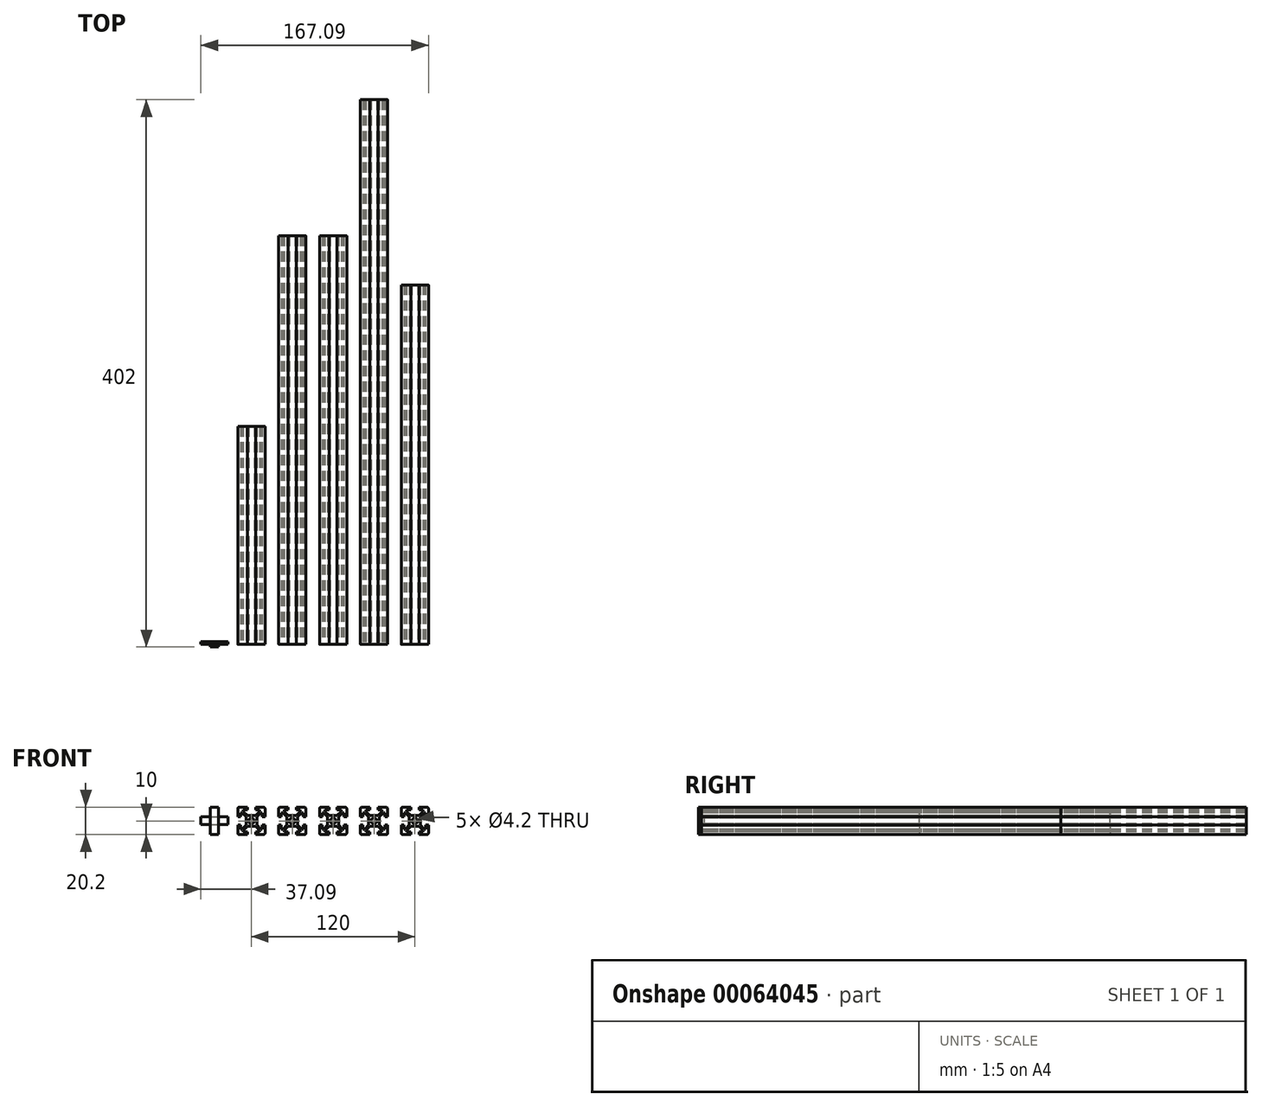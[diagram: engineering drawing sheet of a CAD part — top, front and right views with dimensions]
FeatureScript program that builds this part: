
annotation { "Feature Type Name" : "Feature", "Feature Type Description" : "" }
export const myFeature = defineFeature(function(context is Context, id is Id, definition is map)
    precondition{}
    {
        {
            var Q0;
            Q0=qCreatedBy(makeId("Front.planeOp"),FACE);
            var sketch = newSketch(context, id + "F0", { "sketchPlane" : qUnion([Q0])});
            skLineSegment(sketch, "E0", {"start": v(0, 4) * mm, "end": v(3, 4) * mm});
            skLineSegment(sketch, "E1", {"start": v(3, 4) * mm, "end": v(6, 7) * mm});
            skLineSegment(sketch, "E2", {"start": v(6, 7) * mm, "end": v(6, 8) * mm});
            skLineSegment(sketch, "E3", {"start": v(6, 8) * mm, "end": v(3, 8) * mm});
            skLineSegment(sketch, "E4", {"start": v(3, 8) * mm, "end": v(3, 10) * mm});
            skLineSegment(sketch, "E5", {"start": v(3, 10) * mm, "end": v(9, 10) * mm});
            skLineSegment(sketch, "E6", {"start": v(0, 0) * mm, "end": v(12.93, 12.93) * mm, "construction": true});
            skLineSegment(sketch, "E7.MirrorCS", {"start": v(4, 0) * mm, "end": v(4, 3) * mm});
            skLineSegment(sketch, "E8.MirrorCS", {"start": v(10, 3) * mm, "end": v(10, 9) * mm});
            skLineSegment(sketch, "E9.MirrorCS", {"start": v(8, 3) * mm, "end": v(10, 3) * mm});
            skLineSegment(sketch, "E10.MirrorCS", {"start": v(8, 6) * mm, "end": v(8, 3) * mm});
            skLineSegment(sketch, "E11.MirrorCS", {"start": v(4, 3) * mm, "end": v(7, 6) * mm});
            skLineSegment(sketch, "E12.MirrorCS", {"start": v(7, 6) * mm, "end": v(8, 6) * mm});
            skLineSegment(sketch, "E13.MirrorCS", {"start": v(-8, 3) * mm, "end": v(-10, 3) * mm});
            skLineSegment(sketch, "E14.MirrorCS", {"start": v(0, 4) * mm, "end": v(-3, 4) * mm});
            skLineSegment(sketch, "E15.MirrorCS", {"start": v(-3, 4) * mm, "end": v(-6, 7) * mm});
            skLineSegment(sketch, "E16.MirrorCS", {"start": v(-6, 7) * mm, "end": v(-6, 8) * mm});
            skLineSegment(sketch, "E17.MirrorCS", {"start": v(-6, 8) * mm, "end": v(-3, 8) * mm});
            skLineSegment(sketch, "E18.MirrorCS", {"start": v(-3, 8) * mm, "end": v(-3, 10) * mm});
            skLineSegment(sketch, "E19.MirrorCS", {"start": v(-3, 10) * mm, "end": v(-9, 10) * mm});
            skLineSegment(sketch, "E20.MirrorCS", {"start": v(-4, 0) * mm, "end": v(-4, 3) * mm});
            skLineSegment(sketch, "E21.MirrorCS", {"start": v(-10, 3) * mm, "end": v(-10, 9) * mm});
            skLineSegment(sketch, "E22.MirrorCS", {"start": v(-8, 6) * mm, "end": v(-8, 3) * mm});
            skLineSegment(sketch, "E23.MirrorCS", {"start": v(-4, 3) * mm, "end": v(-7, 6) * mm});
            skLineSegment(sketch, "E24.MirrorCS", {"start": v(-7, 6) * mm, "end": v(-8, 6) * mm});
            skLineSegment(sketch, "E25.MirrorCS", {"start": v(-7, -6) * mm, "end": v(-8, -6) * mm});
            skLineSegment(sketch, "E26.MirrorCS", {"start": v(-6, -7) * mm, "end": v(-6, -8) * mm});
            skLineSegment(sketch, "E27.MirrorCS", {"start": v(6, -7) * mm, "end": v(6, -8) * mm});
            skLineSegment(sketch, "E28.MirrorCS", {"start": v(7, -6) * mm, "end": v(8, -6) * mm});
            skLineSegment(sketch, "E29.MirrorCS", {"start": v(8, -3) * mm, "end": v(10, -3) * mm});
            skLineSegment(sketch, "E30.MirrorCS", {"start": v(-8, -3) * mm, "end": v(-10, -3) * mm});
            skLineSegment(sketch, "E31.MirrorCS", {"start": v(-6, -8) * mm, "end": v(-3, -8) * mm});
            skLineSegment(sketch, "E32.MirrorCS", {"start": v(-3, -10) * mm, "end": v(-9, -10) * mm});
            skLineSegment(sketch, "E33.MirrorCS", {"start": v(-4, -3) * mm, "end": v(-7, -6) * mm});
            skLineSegment(sketch, "E34.MirrorCS", {"start": v(-4, 0) * mm, "end": v(-4, -3) * mm});
            skLineSegment(sketch, "E35.MirrorCS", {"start": v(-3, -8) * mm, "end": v(-3, -10) * mm});
            skLineSegment(sketch, "E36.MirrorCS", {"start": v(0, -4) * mm, "end": v(-3, -4) * mm});
            skLineSegment(sketch, "E37.MirrorCS", {"start": v(0, -4) * mm, "end": v(3, -4) * mm});
            skLineSegment(sketch, "E38.MirrorCS", {"start": v(6, -8) * mm, "end": v(3, -8) * mm});
            skLineSegment(sketch, "E39.MirrorCS", {"start": v(3, -8) * mm, "end": v(3, -10) * mm});
            skLineSegment(sketch, "E40.MirrorCS", {"start": v(3, -10) * mm, "end": v(9, -10) * mm});
            skLineSegment(sketch, "E41.MirrorCS", {"start": v(3, -4) * mm, "end": v(6, -7) * mm});
            skLineSegment(sketch, "E42.MirrorCS", {"start": v(-3, -4) * mm, "end": v(-6, -7) * mm});
            skLineSegment(sketch, "E43.MirrorCS", {"start": v(4, 0) * mm, "end": v(4, -3) * mm});
            skLineSegment(sketch, "E44.MirrorCS", {"start": v(10, -3) * mm, "end": v(10, -9) * mm});
            skLineSegment(sketch, "E45.MirrorCS", {"start": v(8, -6) * mm, "end": v(8, -3) * mm});
            skLineSegment(sketch, "E46.MirrorCS", {"start": v(4, -3) * mm, "end": v(7, -6) * mm});
            skLineSegment(sketch, "E47.MirrorCS", {"start": v(-8, -6) * mm, "end": v(-8, -3) * mm});
            skLineSegment(sketch, "E48.MirrorCS", {"start": v(-10, -3) * mm, "end": v(-10, -9) * mm});
            skCircle(sketch, "E49", {"center": v(0, 0) * mm, "radius": 2.1 * mm});
            skPoint(sketch, "E50.visualSharp", {"position": v(-10, 10) * mm});
            skArc(sketch, "E50.filletArc", {"start": v(-9, 10) * mm, "mid": v(-9.7, 9.7) * mm, "end": v(-10, 9) * mm});
            skPoint(sketch, "E51.visualSharp", {"position": v(10, 10) * mm});
            skArc(sketch, "E51.filletArc", {"start": v(10, 9) * mm, "mid": v(9.7, 9.7) * mm, "end": v(9, 10) * mm});
            skPoint(sketch, "E52.visualSharp", {"position": v(10, -10) * mm});
            skArc(sketch, "E52.filletArc", {"start": v(9, -10) * mm, "mid": v(9.7, -9.7) * mm, "end": v(10, -9) * mm});
            skPoint(sketch, "E53.visualSharp", {"position": v(-10, -10) * mm});
            skArc(sketch, "E53.filletArc", {"start": v(-10, -9) * mm, "mid": v(-9.7, -9.7) * mm, "end": v(-9, -10) * mm});
            skLineSegment(sketch, "E54", {"start": v(-3, 4) * mm, "end": v(-3, 8) * mm, "construction": true});
            skLineSegment(sketch, "E55", {"start": v(3, 4) * mm, "end": v(3, 8) * mm, "construction": true});
            skSolve(sketch);
        }
        {
            var Q0;
            Q0=makeQuery(id+"F0.imprint","IMPRINT",FACE,{"disambiguationData":[TD([[makeQuery(id+"F0.imprint","IMPRINT",EDGE,{"derivedFrom":sQuery(id+"F0.wireOp",EDGE,"E0")}),-1.0]])]});
            extrude(context, id + "F1", {"entities" : qUnion([Q0]), "oppositeDirection" : true, "depth" : 160 * mm});
        }
        {
            var Q0;
            Q0=qSketchRegion(id+"F0",true);
            extrude(context, id + "F2", {"entities" : qUnion([Q0]), "oppositeDirection" : true, "depth" : 300 * mm});
        }
        {
            var Q0;
            Q0=qSketchRegion(id+"F0",true);
            extrude(context, id + "F3", {"entities" : qUnion([Q0]), "oppositeDirection" : true, "depth" : 400 * mm});
        }
        {
            var Q0;
            Q0=makeQuery(id+"F2.opExtrude","SWEPT_BODY",BODY,{"disambiguationData":[OSD([sQuery(id+"F0.wireOp",EDGE,"E0"),sQuery(id+"F0.wireOp",EDGE,"E1"),sQuery(id+"F0.wireOp",EDGE,"E2"),sQuery(id+"F0.wireOp",EDGE,"E3"),sQuery(id+"F0.wireOp",EDGE,"E4"),sQuery(id+"F0.wireOp",EDGE,"E5"),sQuery(id+"F0.wireOp",EDGE,"E7.MirrorCS"),sQuery(id+"F0.wireOp",EDGE,"E8.MirrorCS"),sQuery(id+"F0.wireOp",EDGE,"E10.MirrorCS"),sQuery(id+"F0.wireOp",EDGE,"E11.MirrorCS"),sQuery(id+"F0.wireOp",EDGE,"E12.MirrorCS"),sQuery(id+"F0.wireOp",EDGE,"E9.MirrorCS"),sQuery(id+"F0.wireOp",EDGE,"E14.MirrorCS"),sQuery(id+"F0.wireOp",EDGE,"E15.MirrorCS"),sQuery(id+"F0.wireOp",EDGE,"E16.MirrorCS"),sQuery(id+"F0.wireOp",EDGE,"E17.MirrorCS"),sQuery(id+"F0.wireOp",EDGE,"E18.MirrorCS"),sQuery(id+"F0.wireOp",EDGE,"E19.MirrorCS"),sQuery(id+"F0.wireOp",EDGE,"E20.MirrorCS"),sQuery(id+"F0.wireOp",EDGE,"E21.MirrorCS"),sQuery(id+"F0.wireOp",EDGE,"E22.MirrorCS"),sQuery(id+"F0.wireOp",EDGE,"E23.MirrorCS"),sQuery(id+"F0.wireOp",EDGE,"E13.MirrorCS"),sQuery(id+"F0.wireOp",EDGE,"E24.MirrorCS"),sQuery(id+"F0.wireOp",EDGE,"E25.MirrorCS"),sQuery(id+"F0.wireOp",EDGE,"E26.MirrorCS"),sQuery(id+"F0.wireOp",EDGE,"E27.MirrorCS"),sQuery(id+"F0.wireOp",EDGE,"E28.MirrorCS"),sQuery(id+"F0.wireOp",EDGE,"E31.MirrorCS"),sQuery(id+"F0.wireOp",EDGE,"E32.MirrorCS"),sQuery(id+"F0.wireOp",EDGE,"E33.MirrorCS"),sQuery(id+"F0.wireOp",EDGE,"E34.MirrorCS"),sQuery(id+"F0.wireOp",EDGE,"E35.MirrorCS"),sQuery(id+"F0.wireOp",EDGE,"E36.MirrorCS"),sQuery(id+"F0.wireOp",EDGE,"E37.MirrorCS"),sQuery(id+"F0.wireOp",EDGE,"E38.MirrorCS"),sQuery(id+"F0.wireOp",EDGE,"E39.MirrorCS"),sQuery(id+"F0.wireOp",EDGE,"E40.MirrorCS"),sQuery(id+"F0.wireOp",EDGE,"E41.MirrorCS"),sQuery(id+"F0.wireOp",EDGE,"E42.MirrorCS"),sQuery(id+"F0.wireOp",EDGE,"E43.MirrorCS"),sQuery(id+"F0.wireOp",EDGE,"E44.MirrorCS"),sQuery(id+"F0.wireOp",EDGE,"E29.MirrorCS"),sQuery(id+"F0.wireOp",EDGE,"E45.MirrorCS"),sQuery(id+"F0.wireOp",EDGE,"E46.MirrorCS"),sQuery(id+"F0.wireOp",EDGE,"E47.MirrorCS"),sQuery(id+"F0.wireOp",EDGE,"E48.MirrorCS"),sQuery(id+"F0.wireOp",EDGE,"E30.MirrorCS"),sQuery(id+"F0.wireOp",EDGE,"E49"),sQuery(id+"F0.wireOp",EDGE,"E50.filletArc"),sQuery(id+"F0.wireOp",EDGE,"E51.filletArc"),sQuery(id+"F0.wireOp",EDGE,"E52.filletArc"),sQuery(id+"F0.wireOp",EDGE,"E53.filletArc")])]});
            transform(context, id + "F4", {"entities" : qUnion([Q0]), "transformType" : TransformType.TRANSLATION_3D, "dx" : 60 * mm, "dy" : 0 * mm, "dz" : 0 * mm, "makeCopy" : false});
        }
        {
            var Q0;
            Q0=makeQuery(id+"F3.opExtrude","SWEPT_BODY",BODY,{"disambiguationData":[OSD([sQuery(id+"F0.wireOp",EDGE,"E0"),sQuery(id+"F0.wireOp",EDGE,"E1"),sQuery(id+"F0.wireOp",EDGE,"E2"),sQuery(id+"F0.wireOp",EDGE,"E3"),sQuery(id+"F0.wireOp",EDGE,"E4"),sQuery(id+"F0.wireOp",EDGE,"E5"),sQuery(id+"F0.wireOp",EDGE,"E7.MirrorCS"),sQuery(id+"F0.wireOp",EDGE,"E8.MirrorCS"),sQuery(id+"F0.wireOp",EDGE,"E10.MirrorCS"),sQuery(id+"F0.wireOp",EDGE,"E11.MirrorCS"),sQuery(id+"F0.wireOp",EDGE,"E12.MirrorCS"),sQuery(id+"F0.wireOp",EDGE,"E9.MirrorCS"),sQuery(id+"F0.wireOp",EDGE,"E14.MirrorCS"),sQuery(id+"F0.wireOp",EDGE,"E15.MirrorCS"),sQuery(id+"F0.wireOp",EDGE,"E16.MirrorCS"),sQuery(id+"F0.wireOp",EDGE,"E17.MirrorCS"),sQuery(id+"F0.wireOp",EDGE,"E18.MirrorCS"),sQuery(id+"F0.wireOp",EDGE,"E19.MirrorCS"),sQuery(id+"F0.wireOp",EDGE,"E20.MirrorCS"),sQuery(id+"F0.wireOp",EDGE,"E21.MirrorCS"),sQuery(id+"F0.wireOp",EDGE,"E22.MirrorCS"),sQuery(id+"F0.wireOp",EDGE,"E23.MirrorCS"),sQuery(id+"F0.wireOp",EDGE,"E13.MirrorCS"),sQuery(id+"F0.wireOp",EDGE,"E24.MirrorCS"),sQuery(id+"F0.wireOp",EDGE,"E25.MirrorCS"),sQuery(id+"F0.wireOp",EDGE,"E26.MirrorCS"),sQuery(id+"F0.wireOp",EDGE,"E27.MirrorCS"),sQuery(id+"F0.wireOp",EDGE,"E28.MirrorCS"),sQuery(id+"F0.wireOp",EDGE,"E31.MirrorCS"),sQuery(id+"F0.wireOp",EDGE,"E32.MirrorCS"),sQuery(id+"F0.wireOp",EDGE,"E33.MirrorCS"),sQuery(id+"F0.wireOp",EDGE,"E34.MirrorCS"),sQuery(id+"F0.wireOp",EDGE,"E35.MirrorCS"),sQuery(id+"F0.wireOp",EDGE,"E36.MirrorCS"),sQuery(id+"F0.wireOp",EDGE,"E37.MirrorCS"),sQuery(id+"F0.wireOp",EDGE,"E38.MirrorCS"),sQuery(id+"F0.wireOp",EDGE,"E39.MirrorCS"),sQuery(id+"F0.wireOp",EDGE,"E40.MirrorCS"),sQuery(id+"F0.wireOp",EDGE,"E41.MirrorCS"),sQuery(id+"F0.wireOp",EDGE,"E42.MirrorCS"),sQuery(id+"F0.wireOp",EDGE,"E43.MirrorCS"),sQuery(id+"F0.wireOp",EDGE,"E44.MirrorCS"),sQuery(id+"F0.wireOp",EDGE,"E29.MirrorCS"),sQuery(id+"F0.wireOp",EDGE,"E45.MirrorCS"),sQuery(id+"F0.wireOp",EDGE,"E46.MirrorCS"),sQuery(id+"F0.wireOp",EDGE,"E47.MirrorCS"),sQuery(id+"F0.wireOp",EDGE,"E48.MirrorCS"),sQuery(id+"F0.wireOp",EDGE,"E30.MirrorCS"),sQuery(id+"F0.wireOp",EDGE,"E49"),sQuery(id+"F0.wireOp",EDGE,"E50.filletArc"),sQuery(id+"F0.wireOp",EDGE,"E51.filletArc"),sQuery(id+"F0.wireOp",EDGE,"E52.filletArc"),sQuery(id+"F0.wireOp",EDGE,"E53.filletArc")])]});
            transform(context, id + "F5", {"entities" : qUnion([Q0]), "transformType" : TransformType.TRANSLATION_3D, "dx" : 90 * mm, "dy" : 0 * mm, "dz" : 0 * mm, "makeCopy" : false});
        }
        {
            var Q0;
            Q0=qCreatedBy(makeId("Front.planeOp"),FACE);
            var sketch = newSketch(context, id + "F6", { "sketchPlane" : qUnion([Q0])});
            skLineSegment(sketch, "E56.bottom", {"start": v(-37.1, 10.2) * mm, "end": v(-17.1, 10.2) * mm});
            skLineSegment(sketch, "E56.top", {"start": v(-37.1, -9.8) * mm, "end": v(-17.1, -9.8) * mm});
            skLineSegment(sketch, "E56.left", {"start": v(-37.1, 10.2) * mm, "end": v(-37.1, -9.8) * mm});
            skLineSegment(sketch, "E56.right", {"start": v(-17.1, 10.2) * mm, "end": v(-17.1, -9.8) * mm});
            skLineSegment(sketch, "E57", {"start": v(-30.1, 10.2) * mm, "end": v(-30.1, -9.8) * mm});
            skLineSegment(sketch, "E58", {"start": v(-24.1, 10.2) * mm, "end": v(-24.1, -9.8) * mm});
            skLineSegment(sketch, "E59", {"start": v(-37.1, -2.8) * mm, "end": v(-17.1, -2.8) * mm});
            skLineSegment(sketch, "E60", {"start": v(-37.1, 3.2) * mm, "end": v(-17.1, 3.2) * mm});
            skLineSegment(sketch, "E61", {"start": v(-30.1, 3.2) * mm, "end": v(-24.1, -2.8) * mm, "construction": true});
            skLineSegment(sketch, "E62", {"start": v(-24.1, 3.2) * mm, "end": v(-30.1, -2.8) * mm, "construction": true});
            skPoint(sketch, "E63", {"position": v(-27.1, 0.2) * mm});
            skSolve(sketch);
        }
        {
            var Q0;
            {var subQ3=sQuery(id+"F6.wireOp",EDGE,"E57");var subQ5=sQuery(id+"F6.wireOp",EDGE,"E56.bottom");var subQ7=makeQuery(id+"F6.imprint","INTERSECT",VERTEX,{"derivedFrom":[subQ5,subQ3]});Q0=makeQuery(id+"F6.imprint","IMPRINT",FACE,{"disambiguationData":[TD([[makeQuery(id+"F6.imprint","IMPRINT",EDGE,{"disambiguationData":[TD([[subQ7,-1.0]])],"derivedFrom":subQ5}),-1.0]])]});}
            var Q1;
            {var subQ0=sQuery(id+"F6.wireOp",EDGE,"E60");var subQ3=sQuery(id+"F6.wireOp",EDGE,"E57");var subQ4=makeQuery(id+"F6.imprint","INTERSECT",VERTEX,{"derivedFrom":[subQ3,subQ0]});Q1=makeQuery(id+"F6.imprint","IMPRINT",FACE,{"disambiguationData":[TD([[makeQuery(id+"F6.imprint","IMPRINT",EDGE,{"disambiguationData":[TD([[subQ4,-1.0]])],"derivedFrom":subQ3}),1.0]])]});}
            var Q2;
            {var subQ3=sQuery(id+"F6.wireOp",EDGE,"E57");var subQ5=sQuery(id+"F6.wireOp",EDGE,"E56.top");var subQ7=makeQuery(id+"F6.imprint","INTERSECT",VERTEX,{"derivedFrom":[subQ5,subQ3]});Q2=makeQuery(id+"F6.imprint","IMPRINT",FACE,{"disambiguationData":[TD([[makeQuery(id+"F6.imprint","IMPRINT",EDGE,{"disambiguationData":[TD([[subQ7,-1.0]])],"derivedFrom":subQ5}),1.0]])]});}
            extrude(context, id + "F7", {"entities" : qUnion([Q0, Q1, Q2]), "depth" : 2 * mm});
        }
        {
            var Q0;
            {var subQ3=sQuery(id+"F6.wireOp",EDGE,"E56.left");var subQ5=sQuery(id+"F6.wireOp",EDGE,"E59");var subQ7=makeQuery(id+"F6.imprint","INTERSECT",VERTEX,{"derivedFrom":[subQ3,subQ5]});Q0=makeQuery(id+"F6.imprint","IMPRINT",FACE,{"disambiguationData":[TD([[makeQuery(id+"F6.imprint","IMPRINT",EDGE,{"disambiguationData":[TD([[subQ7,1.0]])],"derivedFrom":subQ3}),1.0]])]});}
            var Q1;
            {var subQ0=sQuery(id+"F6.wireOp",EDGE,"E60");var subQ3=sQuery(id+"F6.wireOp",EDGE,"E57");var subQ4=makeQuery(id+"F6.imprint","INTERSECT",VERTEX,{"derivedFrom":[subQ3,subQ0]});Q1=makeQuery(id+"F6.imprint","IMPRINT",FACE,{"disambiguationData":[TD([[makeQuery(id+"F6.imprint","IMPRINT",EDGE,{"disambiguationData":[TD([[subQ4,-1.0]])],"derivedFrom":subQ3}),1.0]])]});}
            var Q2;
            {var subQ3=sQuery(id+"F6.wireOp",EDGE,"E56.right");var subQ5=sQuery(id+"F6.wireOp",EDGE,"E59");var subQ7=makeQuery(id+"F6.imprint","INTERSECT",VERTEX,{"derivedFrom":[subQ3,subQ5]});Q2=makeQuery(id+"F6.imprint","IMPRINT",FACE,{"disambiguationData":[TD([[makeQuery(id+"F6.imprint","IMPRINT",EDGE,{"disambiguationData":[TD([[subQ7,1.0]])],"derivedFrom":subQ3}),-1.0]])]});}
            extrude(context, id + "F8", {"entities" : qUnion([Q0, Q1, Q2]), "operationType" : NewBodyOperationType.ADD, "oppositeDirection" : true, "depth" : 2 * mm});
        }
        {
            var Q0;
            Q0=makeQuery(id+"F2.opExtrude","SWEPT_FACE",FACE,{"disambiguationData":[OSD([sQuery(id+"F0.wireOp",EDGE,"E5")])]});
            var sketch = newSketch(context, id + "F9", { "sketchPlane" : qUnion([Q0])});
            skLineSegment(sketch, "E64.0", {"start": v(50, 300) * mm, "end": v(50, 0) * mm, "construction": true});
            skLineSegment(sketch, "E65.1", {"start": v(70, 300) * mm, "end": v(70, 0) * mm, "construction": true});
            skLineSegment(sketch, "E66", {"start": v(50, 150) * mm, "end": v(70, 150) * mm, "construction": true});
            skPoint(sketch, "E67", {"position": v(60, 150) * mm});
            skPoint(sketch, "E68", {"position": v(33.74, 152.67) * mm});
            skLineSegment(sketch, "E69", {"start": v(60, 70) * mm, "end": v(60, 230) * mm, "construction": true});
            skPoint(sketch, "E70", {"position": v(60, 70) * mm});
            skPoint(sketch, "E71", {"position": v(60, 230) * mm});
            skPoint(sketch, "E72", {"position": v(27.74, 198.96) * mm});
            skSolve(sketch);
        }
        {
            var Q0;
            Q0=makeQuery(id+"F3.opExtrude","SWEPT_FACE",FACE,{"disambiguationData":[OSD([sQuery(id+"F0.wireOp",EDGE,"E19.MirrorCS")])]});
            var sketch = newSketch(context, id + "F10", { "sketchPlane" : qUnion([Q0])});
            skLineSegment(sketch, "E73", {"start": v(90, 0) * mm, "end": v(90, 10) * mm, "construction": true});
            skPoint(sketch, "E74", {"position": v(90, 390) * mm});
            skLineSegment(sketch, "E75", {"start": v(80, 200) * mm, "end": v(100, 200) * mm, "construction": true});
            skLineSegment(sketch, "E76.1", {"start": v(100, 400) * mm, "end": v(100, 0) * mm, "construction": true});
            skLineSegment(sketch, "E77.1", {"start": v(80, 400) * mm, "end": v(80, 0) * mm, "construction": true});
            skPoint(sketch, "E78", {"position": v(90, 200) * mm});
            skSolve(sketch);
        }
        {
            var Q0;
            Q0=qSketchRegion(id+"F0",true);
            extrude(context, id + "F11", {"entities" : qUnion([Q0]), "oppositeDirection" : true, "depth" : 300 * mm});
        }
        {
            var Q0;
            Q0=makeQuery(id+"F11.opExtrude","SWEPT_BODY",BODY,{"disambiguationData":[OSD([sQuery(id+"F0.wireOp",EDGE,"E0"),sQuery(id+"F0.wireOp",EDGE,"E1"),sQuery(id+"F0.wireOp",EDGE,"E2"),sQuery(id+"F0.wireOp",EDGE,"E3"),sQuery(id+"F0.wireOp",EDGE,"E4"),sQuery(id+"F0.wireOp",EDGE,"E5"),sQuery(id+"F0.wireOp",EDGE,"E7.MirrorCS"),sQuery(id+"F0.wireOp",EDGE,"E8.MirrorCS"),sQuery(id+"F0.wireOp",EDGE,"E10.MirrorCS"),sQuery(id+"F0.wireOp",EDGE,"E11.MirrorCS"),sQuery(id+"F0.wireOp",EDGE,"E12.MirrorCS"),sQuery(id+"F0.wireOp",EDGE,"E9.MirrorCS"),sQuery(id+"F0.wireOp",EDGE,"E14.MirrorCS"),sQuery(id+"F0.wireOp",EDGE,"E15.MirrorCS"),sQuery(id+"F0.wireOp",EDGE,"E16.MirrorCS"),sQuery(id+"F0.wireOp",EDGE,"E17.MirrorCS"),sQuery(id+"F0.wireOp",EDGE,"E18.MirrorCS"),sQuery(id+"F0.wireOp",EDGE,"E19.MirrorCS"),sQuery(id+"F0.wireOp",EDGE,"E20.MirrorCS"),sQuery(id+"F0.wireOp",EDGE,"E21.MirrorCS"),sQuery(id+"F0.wireOp",EDGE,"E22.MirrorCS"),sQuery(id+"F0.wireOp",EDGE,"E23.MirrorCS"),sQuery(id+"F0.wireOp",EDGE,"E13.MirrorCS"),sQuery(id+"F0.wireOp",EDGE,"E24.MirrorCS"),sQuery(id+"F0.wireOp",EDGE,"E25.MirrorCS"),sQuery(id+"F0.wireOp",EDGE,"E26.MirrorCS"),sQuery(id+"F0.wireOp",EDGE,"E27.MirrorCS"),sQuery(id+"F0.wireOp",EDGE,"E28.MirrorCS"),sQuery(id+"F0.wireOp",EDGE,"E31.MirrorCS"),sQuery(id+"F0.wireOp",EDGE,"E32.MirrorCS"),sQuery(id+"F0.wireOp",EDGE,"E33.MirrorCS"),sQuery(id+"F0.wireOp",EDGE,"E34.MirrorCS"),sQuery(id+"F0.wireOp",EDGE,"E35.MirrorCS"),sQuery(id+"F0.wireOp",EDGE,"E36.MirrorCS"),sQuery(id+"F0.wireOp",EDGE,"E37.MirrorCS"),sQuery(id+"F0.wireOp",EDGE,"E38.MirrorCS"),sQuery(id+"F0.wireOp",EDGE,"E39.MirrorCS"),sQuery(id+"F0.wireOp",EDGE,"E40.MirrorCS"),sQuery(id+"F0.wireOp",EDGE,"E41.MirrorCS"),sQuery(id+"F0.wireOp",EDGE,"E42.MirrorCS"),sQuery(id+"F0.wireOp",EDGE,"E43.MirrorCS"),sQuery(id+"F0.wireOp",EDGE,"E44.MirrorCS"),sQuery(id+"F0.wireOp",EDGE,"E29.MirrorCS"),sQuery(id+"F0.wireOp",EDGE,"E45.MirrorCS"),sQuery(id+"F0.wireOp",EDGE,"E46.MirrorCS"),sQuery(id+"F0.wireOp",EDGE,"E47.MirrorCS"),sQuery(id+"F0.wireOp",EDGE,"E48.MirrorCS"),sQuery(id+"F0.wireOp",EDGE,"E30.MirrorCS"),sQuery(id+"F0.wireOp",EDGE,"E49"),sQuery(id+"F0.wireOp",EDGE,"E50.filletArc"),sQuery(id+"F0.wireOp",EDGE,"E51.filletArc"),sQuery(id+"F0.wireOp",EDGE,"E52.filletArc"),sQuery(id+"F0.wireOp",EDGE,"E53.filletArc")])]});
            transform(context, id + "F12", {"entities" : qUnion([Q0]), "transformType" : TransformType.TRANSLATION_3D, "dx" : 30 * mm, "dy" : 0 * mm, "dz" : 0 * mm, "makeCopy" : false});
        }
        {
            var Q0;
            Q0=qSketchRegion(id+"F0",true);
            extrude(context, id + "F13", {"entities" : qUnion([Q0]), "oppositeDirection" : true, "depth" : (300 - (18 * 2)) * mm});
        }
        {
            var Q0;
            Q0=makeQuery(id+"F13.opExtrude","SWEPT_BODY",BODY,{"disambiguationData":[OSD([sQuery(id+"F0.wireOp",EDGE,"E0"),sQuery(id+"F0.wireOp",EDGE,"E1"),sQuery(id+"F0.wireOp",EDGE,"E2"),sQuery(id+"F0.wireOp",EDGE,"E3"),sQuery(id+"F0.wireOp",EDGE,"E4"),sQuery(id+"F0.wireOp",EDGE,"E5"),sQuery(id+"F0.wireOp",EDGE,"E7.MirrorCS"),sQuery(id+"F0.wireOp",EDGE,"E8.MirrorCS"),sQuery(id+"F0.wireOp",EDGE,"E10.MirrorCS"),sQuery(id+"F0.wireOp",EDGE,"E11.MirrorCS"),sQuery(id+"F0.wireOp",EDGE,"E12.MirrorCS"),sQuery(id+"F0.wireOp",EDGE,"E9.MirrorCS"),sQuery(id+"F0.wireOp",EDGE,"E14.MirrorCS"),sQuery(id+"F0.wireOp",EDGE,"E15.MirrorCS"),sQuery(id+"F0.wireOp",EDGE,"E16.MirrorCS"),sQuery(id+"F0.wireOp",EDGE,"E17.MirrorCS"),sQuery(id+"F0.wireOp",EDGE,"E18.MirrorCS"),sQuery(id+"F0.wireOp",EDGE,"E19.MirrorCS"),sQuery(id+"F0.wireOp",EDGE,"E20.MirrorCS"),sQuery(id+"F0.wireOp",EDGE,"E21.MirrorCS"),sQuery(id+"F0.wireOp",EDGE,"E22.MirrorCS"),sQuery(id+"F0.wireOp",EDGE,"E23.MirrorCS"),sQuery(id+"F0.wireOp",EDGE,"E13.MirrorCS"),sQuery(id+"F0.wireOp",EDGE,"E24.MirrorCS"),sQuery(id+"F0.wireOp",EDGE,"E25.MirrorCS"),sQuery(id+"F0.wireOp",EDGE,"E26.MirrorCS"),sQuery(id+"F0.wireOp",EDGE,"E27.MirrorCS"),sQuery(id+"F0.wireOp",EDGE,"E28.MirrorCS"),sQuery(id+"F0.wireOp",EDGE,"E31.MirrorCS"),sQuery(id+"F0.wireOp",EDGE,"E32.MirrorCS"),sQuery(id+"F0.wireOp",EDGE,"E33.MirrorCS"),sQuery(id+"F0.wireOp",EDGE,"E34.MirrorCS"),sQuery(id+"F0.wireOp",EDGE,"E35.MirrorCS"),sQuery(id+"F0.wireOp",EDGE,"E36.MirrorCS"),sQuery(id+"F0.wireOp",EDGE,"E37.MirrorCS"),sQuery(id+"F0.wireOp",EDGE,"E38.MirrorCS"),sQuery(id+"F0.wireOp",EDGE,"E39.MirrorCS"),sQuery(id+"F0.wireOp",EDGE,"E40.MirrorCS"),sQuery(id+"F0.wireOp",EDGE,"E41.MirrorCS"),sQuery(id+"F0.wireOp",EDGE,"E42.MirrorCS"),sQuery(id+"F0.wireOp",EDGE,"E43.MirrorCS"),sQuery(id+"F0.wireOp",EDGE,"E44.MirrorCS"),sQuery(id+"F0.wireOp",EDGE,"E29.MirrorCS"),sQuery(id+"F0.wireOp",EDGE,"E45.MirrorCS"),sQuery(id+"F0.wireOp",EDGE,"E46.MirrorCS"),sQuery(id+"F0.wireOp",EDGE,"E47.MirrorCS"),sQuery(id+"F0.wireOp",EDGE,"E48.MirrorCS"),sQuery(id+"F0.wireOp",EDGE,"E30.MirrorCS"),sQuery(id+"F0.wireOp",EDGE,"E49"),sQuery(id+"F0.wireOp",EDGE,"E50.filletArc"),sQuery(id+"F0.wireOp",EDGE,"E51.filletArc"),sQuery(id+"F0.wireOp",EDGE,"E52.filletArc"),sQuery(id+"F0.wireOp",EDGE,"E53.filletArc")])]});
            transform(context, id + "F14", {"entities" : qUnion([Q0]), "transformType" : TransformType.TRANSLATION_3D, "dx" : 120 * mm, "dy" : 0 * mm, "dz" : 0 * mm, "makeCopy" : false});
        }
    });
